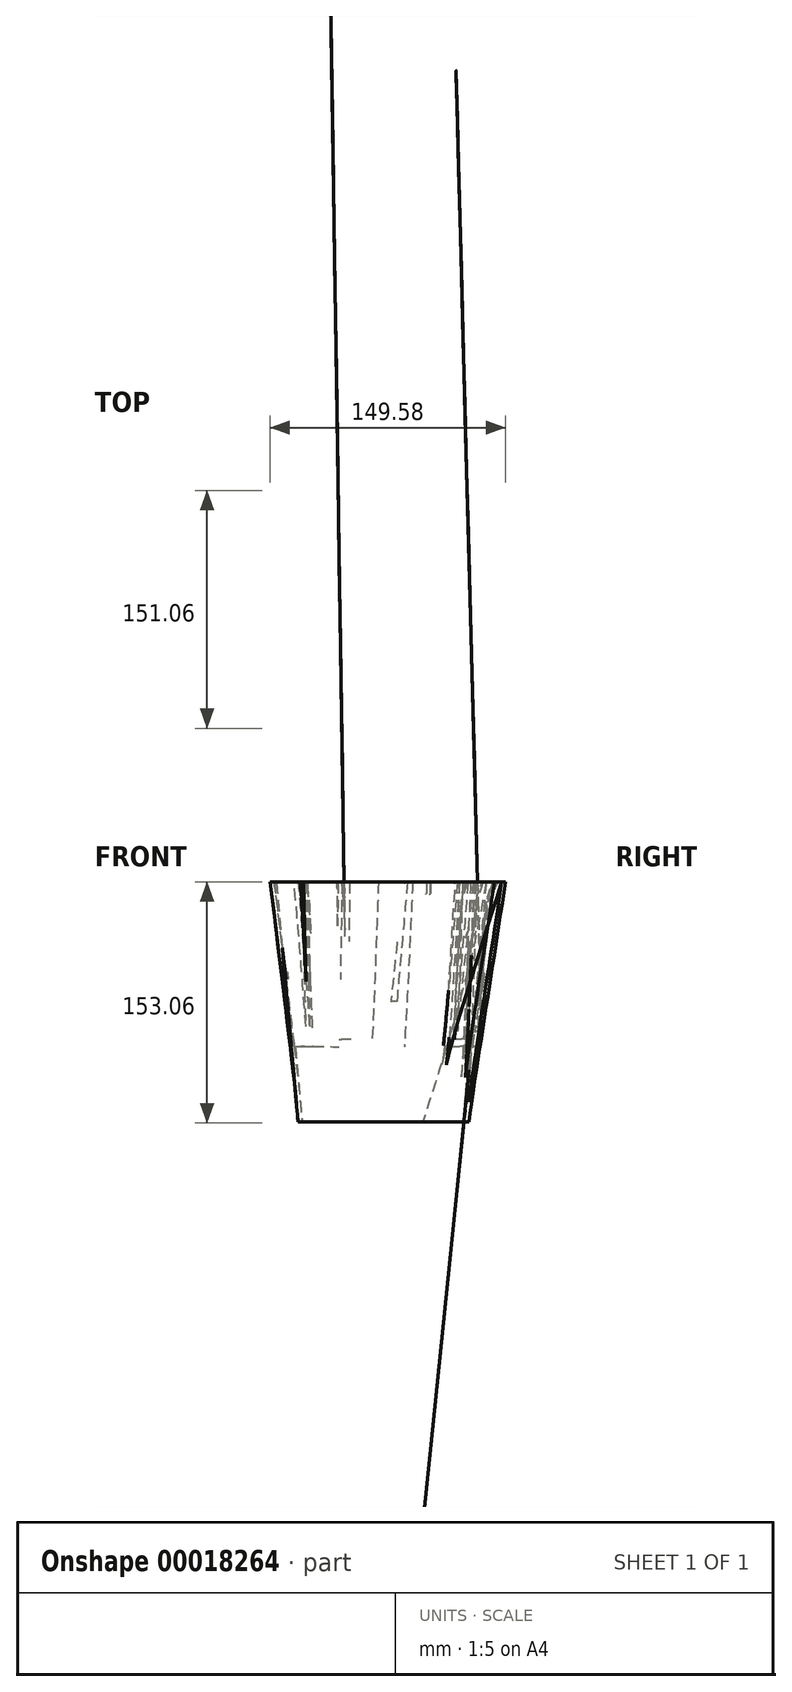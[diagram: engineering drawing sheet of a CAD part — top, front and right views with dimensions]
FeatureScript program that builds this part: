
annotation { "Feature Type Name" : "Feature", "Feature Type Description" : "" }
export const myFeature = defineFeature(function(context is Context, id is Id, definition is map)
    precondition{}
    {
        {
            var Q0;
            Q0=qCreatedBy(makeId("Top.planeOp"),FACE);
            var sketch = newSketch(context, id + "F0", { "sketchPlane" : qUnion([Q0])});
            skCircle(sketch, "E0", {"center": v(0, 0) * mm, "radius": 54.25 * mm});
            skSolve(sketch);
        }
        {
            var Q0;
            Q0=qCreatedBy(makeId("Top.planeOp"),FACE);
            cPlane(context, id + "F1", {"entities" : qUnion([Q0]), "cplaneType" : CPlaneType.OFFSET, "offset" : 152.4 * mm, "width" : 152.4 * mm, "height" : 152.4 * mm});
        }
        {
            var Q0;
            Q0=qCreatedBy(id+"F1.planeOp",FACE);
            var sketch = newSketch(context, id + "F2", { "sketchPlane" : qUnion([Q0])});
            skFitSpline(sketch, "E1", {"points": [v(-68.06, 0) * mm, v(-70, 33.18) * mm, v(-52.56, 30.03) * mm, v(-55.95, 55.47) * mm, v(-30.76, 52.08) * mm, v(-28.82, 70) * mm, v(-10.66, 58.13) * mm, v(0, 74.84) * mm, v(10.9, 57.65) * mm, v(29.07, 73.39) * mm, v(32.94, 48.93) * mm, v(56.68, 59.83) * mm, v(51.6, 32.7) * mm, v(75.09, 24.7) * mm, v(59.83, 8.24) * mm, v(77.5, 0) * mm, v(57.89, -15.99) * mm, v(70.48, -33.42) * mm, v(48.44, -36.33) * mm, v(75.09, -75.33) * mm, v(30.52, -56.68) * mm, v(14.05, -73.15) * mm, v(0, -62.5) * mm, v(-21.8, -76.05) * mm, v(-33.18, -54.01) * mm, v(-51.83, -65.4) * mm, v(-52.56, -30.52) * mm, v(-70.24, -31) * mm, v(-68.06, 0) * mm]});
            skSolve(sketch);
        }
        {
            var Q0;
            Q0=makeQuery(id+"F2.imprint","IMPRINT",FACE,{"disambiguationData":[TD([[makeQuery(id+"F2.imprint","IMPRINT",EDGE,{"derivedFrom":sQuery(id+"F2.wireOp",EDGE,"E1")}),-1.0]])]});
            var Q1;
            Q1=makeQuery(id+"F0.imprint","IMPRINT",FACE,{"disambiguationData":[TD([[makeQuery(id+"F0.imprint","IMPRINT",EDGE,{"derivedFrom":sQuery(id+"F0.wireOp",EDGE,"E0")}),1.0]])]});
            loft(context, id + "F3", {"sheetProfilesArray" : [{ "sheetProfileEntities" : qUnion([Q0]) }, { "sheetProfileEntities" : qUnion([Q1]) }]});
        }
        {
            var Q0;
            Q0=makeQuery(id+"F3.opLoft","CAP_FACE",FACE,{"disambiguationData":[OSD([makeQuery(id+"F0.imprint","IMPRINT",FACE,{"disambiguationData":[TD([[makeQuery(id+"F0.imprint","IMPRINT",EDGE,{"derivedFrom":sQuery(id+"F0.wireOp",EDGE,"E0")}),1.0]])]})])],"isStart":true});
            var Q1;
            Q1=makeQuery(id+"F3.opLoft","CAP_FACE",FACE,{"disambiguationData":[OSD([makeQuery(id+"F2.imprint","IMPRINT",FACE,{"disambiguationData":[TD([[makeQuery(id+"F2.imprint","IMPRINT",EDGE,{"derivedFrom":sQuery(id+"F2.wireOp",EDGE,"E1")}),-1.0]])]})])],"isStart":true});
            shell(context, id + "F4", {"entities" : qUnion([Q0, Q1]), "thickness" : 2.54 * mm});
        }
    });
